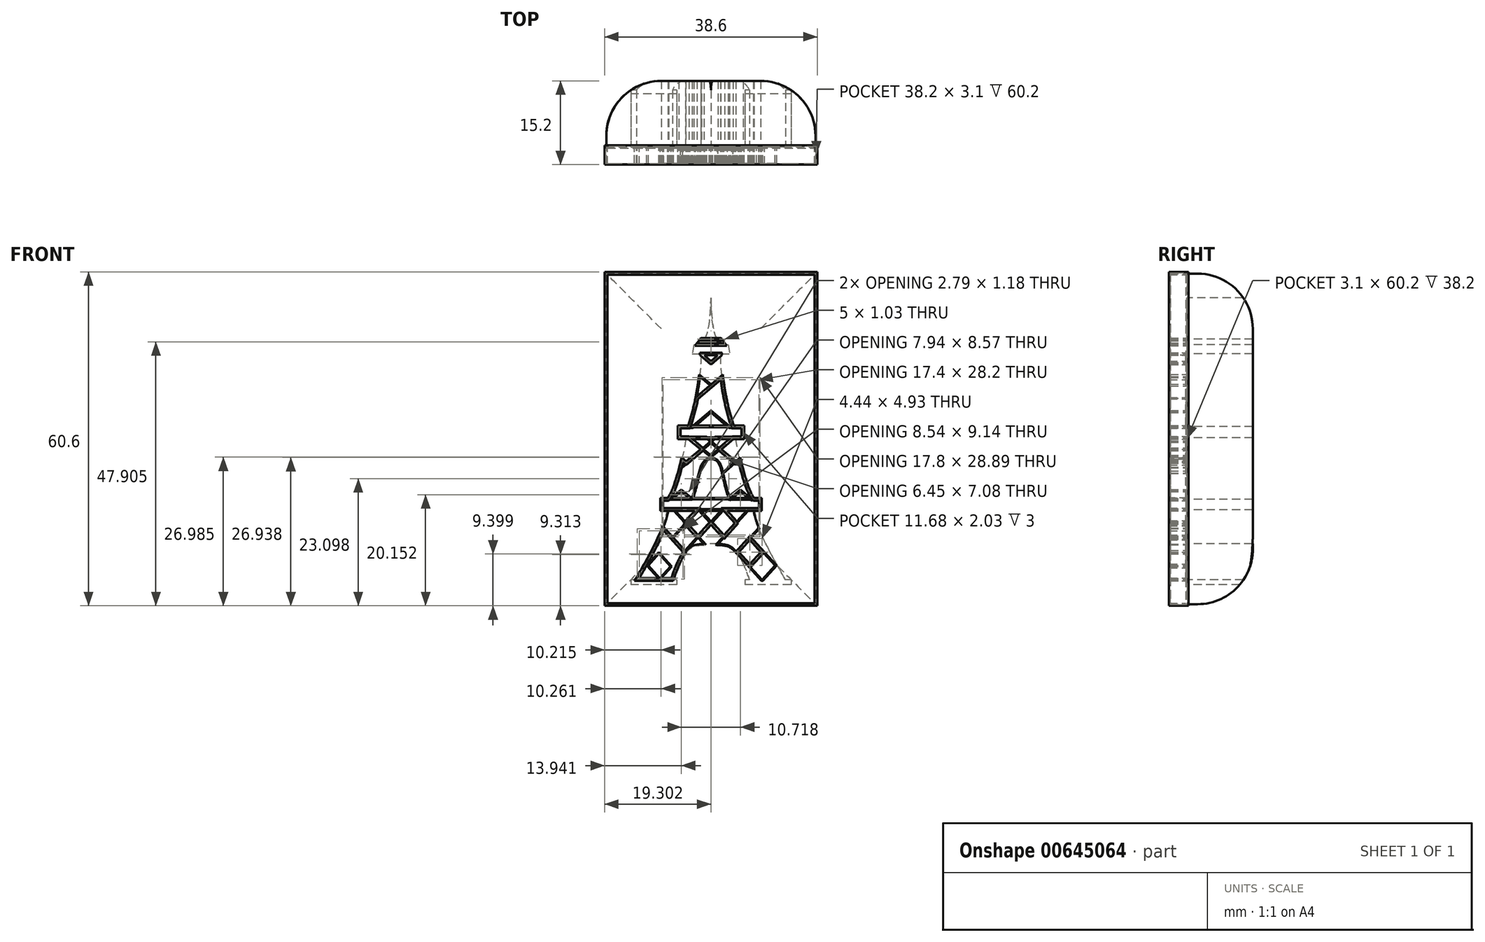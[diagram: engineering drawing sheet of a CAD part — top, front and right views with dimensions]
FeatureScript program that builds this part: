
annotation { "Feature Type Name" : "Feature", "Feature Type Description" : "" }
export const myFeature = defineFeature(function(context is Context, id is Id, definition is map)
    precondition{}
    {
        {
            var Q0;
            Q0=qCreatedBy(makeId("Front.planeOp"),FACE);
            var sketch = newSketch(context, id + "F0", { "sketchPlane" : qUnion([Q0])});
            skLineSegment(sketch, "E0.bottom", {"start": v(-9, 1.93) * mm, "end": v(9, 1.93) * mm});
            skLineSegment(sketch, "E0.top", {"start": v(-9, 0) * mm, "end": v(9, 0) * mm});
            skLineSegment(sketch, "E0.left", {"start": v(-9, 1.93) * mm, "end": v(-9, 0) * mm});
            skLineSegment(sketch, "E0.right", {"start": v(9, 1.93) * mm, "end": v(9, 0) * mm});
            skLineSegment(sketch, "E1.bottom", {"start": v(-5.84, 15.08) * mm, "end": v(5.84, 15.08) * mm});
            skLineSegment(sketch, "E1.top", {"start": v(-5.84, 13.05) * mm, "end": v(5.84, 13.05) * mm});
            skLineSegment(sketch, "E1.left", {"start": v(-5.84, 15.08) * mm, "end": v(-5.84, 13.05) * mm});
            skLineSegment(sketch, "E1.right", {"start": v(5.84, 15.08) * mm, "end": v(5.84, 13.05) * mm});
            skFitSpline(sketch, "E2", {"points": [v(-7.8, 1.93) * mm, v(-4.54, 13.05) * mm], "startDerivative": vector(4.67, 4.81) * mm, "endDerivative": vector(-0.3, 2.62) * mm});
            skFitSpline(sketch, "E3.MirrorCS", {"points": [v(7.8, 1.93) * mm, v(4.54, 13.05) * mm], "startDerivative": vector(-4.67, 4.81) * mm, "endDerivative": vector(0.3, 2.62) * mm});
            skFitSpline(sketch, "E4", {"points": [v(-3.5, 1.93) * mm, v(-1.06, 9.05) * mm, v(1.15, 9.05) * mm, v(3.51, 1.93) * mm], "startDerivative": vector(9.55, 27.67) * mm, "endDerivative": vector(10.37, -28.05) * mm});
            skPoint(sketch, "E5", {"position": v(0, 38.45) * mm});
            skPoint(sketch, "E6", {"position": v(0, -12.7) * mm});
            skLineSegment(sketch, "E7.bottom", {"start": v(-3.1, 29.96) * mm, "end": v(3.1, 29.96) * mm});
            skLineSegment(sketch, "E7.top", {"start": v(-3.4, 28.34) * mm, "end": v(3.4, 28.34) * mm});
            skLineSegment(sketch, "E8", {"start": v(-1.73, 30.99) * mm, "end": v(1.73, 30.99) * mm});
            skLineSegment(sketch, "E9", {"start": v(-2.5, 29.96) * mm, "end": v(2.5, 29.96) * mm});
            skLineSegment(sketch, "E10", {"start": v(-2.5, 29.96) * mm, "end": v(-1.73, 30.99) * mm});
            skLineSegment(sketch, "E11", {"start": v(1.73, 30.99) * mm, "end": v(2.5, 29.96) * mm});
            skFitSpline(sketch, "E12", {"points": [v(-1.28, 30.99) * mm, v(0, 38.45) * mm], "startDerivative": vector(2.63, 2) * mm, "endDerivative": vector(0.25, 11.2) * mm});
            skFitSpline(sketch, "E13.MirrorCS", {"points": [v(1.28, 30.99) * mm, v(0, 38.45) * mm], "startDerivative": vector(-2.63, 2) * mm, "endDerivative": vector(-0.25, 11.2) * mm});
            skLineSegment(sketch, "E14", {"start": v(-3.1, 29.96) * mm, "end": v(-3.4, 28.34) * mm});
            skLineSegment(sketch, "E15", {"start": v(3.1, 29.96) * mm, "end": v(3.4, 28.34) * mm});
            skFitSpline(sketch, "E16", {"points": [v(-4, 15.07) * mm, v(-1.8, 28.35) * mm], "startDerivative": vector(5.02, 14.78) * mm, "endDerivative": vector(-0.5, 7.77) * mm});
            skFitSpline(sketch, "E17.MirrorCS", {"points": [v(4, 15.07) * mm, v(1.8, 28.35) * mm], "startDerivative": vector(-5.02, 14.78) * mm, "endDerivative": vector(0.5, 7.77) * mm});
            skFitSpline(sketch, "E18", {"points": [v(-13.53, -12.7) * mm, v(-7.7, 0) * mm], "startDerivative": vector(10.31, 17.56) * mm, "endDerivative": vector(1.77, 9.43) * mm});
            skFitSpline(sketch, "E19", {"points": [v(-7, -12.7) * mm, v(-1.83, -6.23) * mm, v(1.83, -6.23) * mm, v(7, -12.7) * mm], "startDerivative": vector(16.22, 48.06) * mm, "endDerivative": vector(16.22, -48.06) * mm});
            skFitSpline(sketch, "E20.MirrorCS", {"points": [v(13.53, -12.7) * mm, v(7.7, 0) * mm], "startDerivative": vector(-10.31, 17.56) * mm, "endDerivative": vector(-1.77, 9.43) * mm});
            skLineSegment(sketch, "E21", {"start": v(-13.53, -12.7) * mm, "end": v(-7, -12.7) * mm});
            skLineSegment(sketch, "E22.bottom", {"start": v(-14.53, -12.7) * mm, "end": v(-6.2, -12.7) * mm});
            skLineSegment(sketch, "E22.top", {"start": v(-14.53, -13.6) * mm, "end": v(-6.2, -13.6) * mm});
            skLineSegment(sketch, "E22.left", {"start": v(-14.53, -12.7) * mm, "end": v(-14.53, -13.6) * mm});
            skLineSegment(sketch, "E22.right", {"start": v(-6.2, -12.7) * mm, "end": v(-6.2, -13.6) * mm});
            skLineSegment(sketch, "E23.MirrorCS", {"start": v(14.53, -12.7) * mm, "end": v(14.53, -13.6) * mm});
            skLineSegment(sketch, "E24.MirrorCS", {"start": v(14.53, -12.7) * mm, "end": v(6.2, -12.7) * mm});
            skLineSegment(sketch, "E25.MirrorCS", {"start": v(6.2, -12.7) * mm, "end": v(6.2, -13.6) * mm});
            skLineSegment(sketch, "E26.MirrorCS", {"start": v(14.53, -13.6) * mm, "end": v(6.2, -13.6) * mm});
            skLineSegment(sketch, "E27", {"start": v(-12.7, -11.28) * mm, "end": v(-2.52, 0) * mm});
            skLineSegment(sketch, "E28", {"start": v(-9.27, -12.7) * mm, "end": v(2.2, 0) * mm});
            skLineSegment(sketch, "E29", {"start": v(6.9, 0) * mm, "end": v(1.3, -6.2) * mm});
            skLineSegment(sketch, "E30", {"start": v(4.68, -7.7) * mm, "end": v(8.67, -3.27) * mm});
            skLineSegment(sketch, "E31", {"start": v(6.4, -11.02) * mm, "end": v(10.24, -6.76) * mm});
            skLineSegment(sketch, "E32.MirrorCS", {"start": v(12.7, -11.28) * mm, "end": v(2.52, 0) * mm});
            skLineSegment(sketch, "E33.MirrorCS", {"start": v(9.27, -12.7) * mm, "end": v(-2.2, 0) * mm});
            skLineSegment(sketch, "E34.MirrorCS", {"start": v(-6.9, 0) * mm, "end": v(-1.3, -6.2) * mm});
            skLineSegment(sketch, "E35.MirrorCS", {"start": v(-6.4, -11.02) * mm, "end": v(-10.24, -6.76) * mm});
            skLineSegment(sketch, "E36.MirrorCS", {"start": v(-4.68, -7.7) * mm, "end": v(-8.67, -3.27) * mm});
            skLineSegment(sketch, "E37", {"start": v(7, -12.7) * mm, "end": v(13.53, -12.7) * mm});
            skLineSegment(sketch, "E38", {"start": v(11.89, -9.85) * mm, "end": v(9.31, -12.7) * mm});
            skLineSegment(sketch, "E39.MirrorCS", {"start": v(-11.89, -9.85) * mm, "end": v(-9.31, -12.7) * mm});
            skLineSegment(sketch, "E40", {"start": v(-3.42, 1.93) * mm, "end": v(-6.5, 4.55) * mm});
            skLineSegment(sketch, "E41", {"start": v(-2.22, 6.61) * mm, "end": v(-5.22, 9.15) * mm});
            skLineSegment(sketch, "E42", {"start": v(0.27, 9.4) * mm, "end": v(-4.02, 13.05) * mm});
            skLineSegment(sketch, "E43", {"start": v(5.6, 7.62) * mm, "end": v(-0.8, 13.05) * mm});
            skLineSegment(sketch, "E44", {"start": v(2.33, 6.14) * mm, "end": v(7.3, 1.93) * mm});
            skLineSegment(sketch, "E45.MirrorCS", {"start": v(-2.33, 6.14) * mm, "end": v(-7.3, 1.93) * mm});
            skLineSegment(sketch, "E46.MirrorCS", {"start": v(-5.6, 7.62) * mm, "end": v(0.8, 13.05) * mm});
            skLineSegment(sketch, "E47.MirrorCS", {"start": v(-0.27, 9.4) * mm, "end": v(4.02, 13.05) * mm});
            skLineSegment(sketch, "E48.MirrorCS", {"start": v(2.22, 6.61) * mm, "end": v(5.22, 9.15) * mm});
            skLineSegment(sketch, "E49.MirrorCS", {"start": v(3.42, 1.93) * mm, "end": v(6.5, 4.55) * mm});
            skLineSegment(sketch, "E50", {"start": v(3.33, 15.08) * mm, "end": v(-2.64, 20.15) * mm});
            skLineSegment(sketch, "E51", {"start": v(2.62, 20.28) * mm, "end": v(-2, 24.2) * mm});
            skLineSegment(sketch, "E52", {"start": v(1.9, 25) * mm, "end": v(-1.8, 28.15) * mm});
            skLineSegment(sketch, "E53.MirrorCS", {"start": v(-1.9, 25) * mm, "end": v(1.8, 28.15) * mm});
            skLineSegment(sketch, "E54.MirrorCS", {"start": v(-3.33, 15.08) * mm, "end": v(2.64, 20.15) * mm});
            skLineSegment(sketch, "E55.MirrorCS", {"start": v(-2.62, 20.28) * mm, "end": v(2, 24.2) * mm});
            skLineSegment(sketch, "E56.bottom", {"start": v(-19, 42.87) * mm, "end": v(19, 42.87) * mm});
            skLineSegment(sketch, "E56.top", {"start": v(-19, -17.13) * mm, "end": v(19, -17.13) * mm});
            skLineSegment(sketch, "E56.left", {"start": v(-19, 42.87) * mm, "end": v(-19, -17.13) * mm});
            skLineSegment(sketch, "E56.right", {"start": v(19, 42.87) * mm, "end": v(19, -17.13) * mm});
            skSolve(sketch);
        }
        {
            var Q0;
            {var subQ0=sQuery(id+"F0.wireOp",EDGE,"E12");Q0=makeQuery(id+"F0.imprint","IMPRINT",FACE,{"disambiguationData":[TD([[makeQuery(id+"F0.imprint","IMPRINT",EDGE,{"derivedFrom":subQ0}),-1.0]])]});}
            var Q1;
            Q1=makeQuery(id+"F0.imprint","IMPRINT",FACE,{"disambiguationData":[TD([[makeQuery(id+"F0.imprint","IMPRINT",EDGE,{"derivedFrom":sQuery(id+"F0.wireOp",EDGE,"E7.bottom")}),-1.0]])]});
            var Q2;
            {var subQ5=sQuery(id+"F0.wireOp",EDGE,"E51");var subQ6=sQuery(id+"F0.wireOp",EDGE,"E16");var subQ7=makeQuery(id+"F0.imprint","INTERSECT",VERTEX,{"derivedFrom":[subQ6,subQ5]});Q2=makeQuery(id+"F0.imprint","IMPRINT",FACE,{"disambiguationData":[TD([[makeQuery(id+"F0.imprint","IMPRINT",EDGE,{"disambiguationData":[TD([[subQ7,-1.0]])],"derivedFrom":subQ6}),-1.0]])]});}
            var Q3;
            {var subQ5=sQuery(id+"F0.wireOp",EDGE,"E50");var subQ6=sQuery(id+"F0.wireOp",EDGE,"E16");var subQ7=makeQuery(id+"F0.imprint","INTERSECT",VERTEX,{"derivedFrom":[subQ6,subQ5]});Q3=makeQuery(id+"F0.imprint","IMPRINT",FACE,{"disambiguationData":[TD([[makeQuery(id+"F0.imprint","IMPRINT",EDGE,{"disambiguationData":[TD([[subQ7,-1.0]])],"derivedFrom":subQ6}),-1.0]])]});}
            var Q4;
            {var subQ0=sQuery(id+"F0.wireOp",EDGE,"E50");var subQ1=sQuery(id+"F0.wireOp",EDGE,"E1.bottom");var subQ2=makeQuery(id+"F0.imprint","INTERSECT",VERTEX,{"derivedFrom":[subQ1,subQ0]});Q4=makeQuery(id+"F0.imprint","IMPRINT",FACE,{"disambiguationData":[TD([[makeQuery(id+"F0.imprint","IMPRINT",EDGE,{"disambiguationData":[TD([[subQ2,1.0]])],"derivedFrom":subQ1}),1.0]])]});}
            var Q5;
            {var subQ0=sQuery(id+"F0.wireOp",EDGE,"E43");var subQ1=sQuery(id+"F0.wireOp",EDGE,"E1.top");var subQ2=makeQuery(id+"F0.imprint","INTERSECT",VERTEX,{"derivedFrom":[subQ1,subQ0]});Q5=makeQuery(id+"F0.imprint","IMPRINT",FACE,{"disambiguationData":[TD([[makeQuery(id+"F0.imprint","IMPRINT",EDGE,{"disambiguationData":[TD([[subQ2,-1.0]])],"derivedFrom":subQ1}),-1.0]])]});}
            var Q6;
            {var subQ1=sQuery(id+"F0.wireOp",EDGE,"E2");var subQ6=sQuery(id+"F0.wireOp",EDGE,"E1.top");var subQ9=makeQuery(id+"F0.imprint","INTERSECT",VERTEX,{"derivedFrom":[subQ6,subQ1]});Q6=makeQuery(id+"F0.imprint","IMPRINT",FACE,{"disambiguationData":[TD([[makeQuery(id+"F0.imprint","IMPRINT",EDGE,{"disambiguationData":[TD([[subQ9,-1.0]])],"derivedFrom":subQ6}),-1.0]])]});}
            var Q7;
            {var subQ0=sQuery(id+"F0.wireOp",EDGE,"E47.MirrorCS");var subQ1=sQuery(id+"F0.wireOp",EDGE,"E42");var subQ2=makeQuery(id+"F0.imprint","INTERSECT",VERTEX,{"derivedFrom":[subQ1,subQ0]});Q7=makeQuery(id+"F0.imprint","IMPRINT",FACE,{"disambiguationData":[TD([[makeQuery(id+"F0.imprint","IMPRINT",EDGE,{"disambiguationData":[TD([[subQ2,-1.0]])],"derivedFrom":subQ1}),-1.0]])]});}
            var Q8;
            {var subQ5=sQuery(id+"F0.wireOp",EDGE,"E1.top");var subQ7=sQuery(id+"F0.wireOp",EDGE,"E3.MirrorCS");var subQ8=makeQuery(id+"F0.imprint","INTERSECT",VERTEX,{"derivedFrom":[subQ5,subQ7]});Q8=makeQuery(id+"F0.imprint","IMPRINT",FACE,{"disambiguationData":[TD([[makeQuery(id+"F0.imprint","IMPRINT",EDGE,{"disambiguationData":[TD([[subQ8,1.0]])],"derivedFrom":subQ5}),-1.0]])]});}
            var Q9;
            {var subQ0=sQuery(id+"F0.wireOp",EDGE,"E4");var subQ1=sQuery(id+"F0.wireOp",EDGE,"E0.bottom");var subQ2=makeQuery(id+"F0.imprint","INTERSECT",VERTEX,{"disambiguationData":[OD(1.0)],"derivedFrom":[subQ1,subQ0]});Q9=makeQuery(id+"F0.imprint","IMPRINT",FACE,{"disambiguationData":[TD([[makeQuery(id+"F0.imprint","IMPRINT",EDGE,{"disambiguationData":[TD([[subQ2,-1.0]])],"derivedFrom":subQ1}),1.0]])]});}
            var Q10;
            {var subQ0=sQuery(id+"F0.wireOp",EDGE,"E4");var subQ1=sQuery(id+"F0.wireOp",EDGE,"E0.bottom");var subQ2=makeQuery(id+"F0.imprint","INTERSECT",VERTEX,{"disambiguationData":[OD(0.0)],"derivedFrom":[subQ1,subQ0]});Q10=makeQuery(id+"F0.imprint","IMPRINT",FACE,{"disambiguationData":[TD([[makeQuery(id+"F0.imprint","IMPRINT",EDGE,{"disambiguationData":[TD([[subQ2,1.0]])],"derivedFrom":subQ1}),1.0]])]});}
            var Q11;
            {var subQ0=sQuery(id+"F0.wireOp",EDGE,"E27");var subQ1=sQuery(id+"F0.wireOp",EDGE,"E0.top");var subQ2=makeQuery(id+"F0.imprint","INTERSECT",VERTEX,{"derivedFrom":[subQ1,subQ0]});Q11=makeQuery(id+"F0.imprint","IMPRINT",FACE,{"disambiguationData":[TD([[makeQuery(id+"F0.imprint","IMPRINT",EDGE,{"disambiguationData":[TD([[subQ2,1.0]])],"derivedFrom":subQ1}),-1.0]])]});}
            var Q12;
            {var subQ0=sQuery(id+"F0.wireOp",EDGE,"E29");var subQ1=sQuery(id+"F0.wireOp",EDGE,"E0.top");var subQ2=makeQuery(id+"F0.imprint","INTERSECT",VERTEX,{"derivedFrom":[subQ1,subQ0]});Q12=makeQuery(id+"F0.imprint","IMPRINT",FACE,{"disambiguationData":[TD([[makeQuery(id+"F0.imprint","IMPRINT",EDGE,{"disambiguationData":[TD([[subQ2,1.0]])],"derivedFrom":subQ1}),-1.0]])]});}
            var Q13;
            {var subQ0=sQuery(id+"F0.wireOp",EDGE,"E32.MirrorCS");var subQ1=sQuery(id+"F0.wireOp",EDGE,"E29");var subQ2=makeQuery(id+"F0.imprint","INTERSECT",VERTEX,{"derivedFrom":[subQ1,subQ0]});Q13=makeQuery(id+"F0.imprint","IMPRINT",FACE,{"disambiguationData":[TD([[makeQuery(id+"F0.imprint","IMPRINT",EDGE,{"disambiguationData":[TD([[subQ2,-1.0]])],"derivedFrom":subQ1}),1.0]])]});}
            var Q14;
            {var subQ0=sQuery(id+"F0.wireOp",EDGE,"E28");var subQ1=sQuery(id+"F0.wireOp",EDGE,"E0.top");var subQ2=makeQuery(id+"F0.imprint","INTERSECT",VERTEX,{"derivedFrom":[subQ1,subQ0]});Q14=makeQuery(id+"F0.imprint","IMPRINT",FACE,{"disambiguationData":[TD([[makeQuery(id+"F0.imprint","IMPRINT",EDGE,{"disambiguationData":[TD([[subQ2,1.0]])],"derivedFrom":subQ1}),-1.0]])]});}
            var Q15;
            {var subQ0=sQuery(id+"F0.wireOp",EDGE,"E35.MirrorCS");var subQ1=sQuery(id+"F0.wireOp",EDGE,"E18");var subQ2=makeQuery(id+"F0.imprint","INTERSECT",VERTEX,{"derivedFrom":[subQ1,subQ0]});Q15=makeQuery(id+"F0.imprint","IMPRINT",FACE,{"disambiguationData":[TD([[makeQuery(id+"F0.imprint","IMPRINT",EDGE,{"disambiguationData":[TD([[subQ2,-1.0]])],"derivedFrom":subQ1}),-1.0]])]});}
            var Q16;
            {var subQ0=sQuery(id+"F0.wireOp",EDGE,"E36.MirrorCS");var subQ1=sQuery(id+"F0.wireOp",EDGE,"E27");var subQ2=makeQuery(id+"F0.imprint","INTERSECT",VERTEX,{"derivedFrom":[subQ1,subQ0]});Q16=makeQuery(id+"F0.imprint","IMPRINT",FACE,{"disambiguationData":[TD([[makeQuery(id+"F0.imprint","IMPRINT",EDGE,{"disambiguationData":[TD([[subQ2,-1.0]])],"derivedFrom":subQ1}),-1.0]])]});}
            var Q17;
            {var subQ3=sQuery(id+"F0.wireOp",EDGE,"E29");var subQ5=sQuery(id+"F0.wireOp",EDGE,"E19");var subQ6=makeQuery(id+"F0.imprint","INTERSECT",VERTEX,{"derivedFrom":[subQ5,subQ3]});Q17=makeQuery(id+"F0.imprint","IMPRINT",FACE,{"disambiguationData":[TD([[makeQuery(id+"F0.imprint","IMPRINT",EDGE,{"disambiguationData":[TD([[subQ6,1.0]])],"derivedFrom":subQ5}),1.0]])]});}
            var Q18;
            {var subQ0=sQuery(id+"F0.wireOp",EDGE,"E30");var subQ1=sQuery(id+"F0.wireOp",EDGE,"E20.MirrorCS");var subQ2=makeQuery(id+"F0.imprint","INTERSECT",VERTEX,{"derivedFrom":[subQ1,subQ0]});Q18=makeQuery(id+"F0.imprint","IMPRINT",FACE,{"disambiguationData":[TD([[makeQuery(id+"F0.imprint","IMPRINT",EDGE,{"disambiguationData":[TD([[subQ2,1.0]])],"derivedFrom":subQ1}),1.0]])]});}
            var Q19;
            {var subQ3=sQuery(id+"F0.wireOp",EDGE,"E28");var subQ5=sQuery(id+"F0.wireOp",EDGE,"E22.bottom");var subQ6=makeQuery(id+"F0.imprint","INTERSECT",VERTEX,{"derivedFrom":[subQ5,subQ3]});Q19=makeQuery(id+"F0.imprint","IMPRINT",FACE,{"disambiguationData":[TD([[makeQuery(id+"F0.imprint","IMPRINT",EDGE,{"disambiguationData":[TD([[subQ6,1.0]])],"derivedFrom":subQ5}),1.0]])]});}
            var Q20;
            {var subQ0=sQuery(id+"F0.wireOp",EDGE,"E35.MirrorCS");var subQ1=sQuery(id+"F0.wireOp",EDGE,"E19");var subQ2=makeQuery(id+"F0.imprint","INTERSECT",VERTEX,{"derivedFrom":[subQ1,subQ0]});Q20=makeQuery(id+"F0.imprint","IMPRINT",FACE,{"disambiguationData":[TD([[makeQuery(id+"F0.imprint","IMPRINT",EDGE,{"disambiguationData":[TD([[subQ2,-1.0]])],"derivedFrom":subQ1}),1.0]])]});}
            var Q21;
            {var subQ0=sQuery(id+"F0.wireOp",EDGE,"E30");var subQ1=sQuery(id+"F0.wireOp",EDGE,"E19");var subQ2=makeQuery(id+"F0.imprint","INTERSECT",VERTEX,{"derivedFrom":[subQ1,subQ0]});Q21=makeQuery(id+"F0.imprint","IMPRINT",FACE,{"disambiguationData":[TD([[makeQuery(id+"F0.imprint","IMPRINT",EDGE,{"disambiguationData":[TD([[subQ2,-1.0]])],"derivedFrom":subQ1}),1.0]])]});}
            var Q22;
            {var subQ1=sQuery(id+"F0.wireOp",EDGE,"E33.MirrorCS");var subQ5=sQuery(id+"F0.wireOp",EDGE,"E31");var subQ6=makeQuery(id+"F0.imprint","INTERSECT",VERTEX,{"derivedFrom":[subQ5,subQ1]});Q22=makeQuery(id+"F0.imprint","IMPRINT",FACE,{"disambiguationData":[TD([[makeQuery(id+"F0.imprint","IMPRINT",EDGE,{"disambiguationData":[TD([[subQ6,-1.0]])],"derivedFrom":subQ5}),-1.0]])]});}
            var Q23;
            {var subQ0=sQuery(id+"F0.wireOp",EDGE,"E32.MirrorCS");var subQ1=sQuery(id+"F0.wireOp",EDGE,"E20.MirrorCS");var subQ2=makeQuery(id+"F0.imprint","INTERSECT",VERTEX,{"derivedFrom":[subQ1,subQ0]});Q23=makeQuery(id+"F0.imprint","IMPRINT",FACE,{"disambiguationData":[TD([[makeQuery(id+"F0.imprint","IMPRINT",EDGE,{"disambiguationData":[TD([[subQ2,-1.0]])],"derivedFrom":subQ1}),1.0]])]});}
            var Q24;
            {var subQ0=sQuery(id+"F0.wireOp",EDGE,"E27");var subQ1=sQuery(id+"F0.wireOp",EDGE,"E18");var subQ2=makeQuery(id+"F0.imprint","INTERSECT",VERTEX,{"derivedFrom":[subQ1,subQ0]});Q24=makeQuery(id+"F0.imprint","IMPRINT",FACE,{"disambiguationData":[TD([[makeQuery(id+"F0.imprint","IMPRINT",EDGE,{"disambiguationData":[TD([[subQ2,-1.0]])],"derivedFrom":subQ1}),-1.0]])]});}
            var Q25;
            Q25=makeQuery(id+"F0.imprint","IMPRINT",FACE,{"disambiguationData":[TD([[makeQuery(id+"F0.imprint","IMPRINT",EDGE,{"derivedFrom":sQuery(id+"F0.wireOp",EDGE,"E22.top")}),1.0]])]});
            var Q26;
            {var subQ5=sQuery(id+"F0.wireOp",EDGE,"E23.MirrorCS");Q26=makeQuery(id+"F0.imprint","IMPRINT",FACE,{"disambiguationData":[TD([[makeQuery(id+"F0.imprint","IMPRINT",EDGE,{"derivedFrom":subQ5}),-1.0]])]});}
            extrude(context, id + "F1", {"entities" : qUnion([Q0, Q1, Q2, Q3, Q4, Q5, Q6, Q7, Q8, Q9, Q10, Q11, Q12, Q13, Q14, Q15, Q16, Q17, Q18, Q19, Q20, Q21, Q22, Q23, Q24, Q25, Q26]), "depth" : 3 * mm, "offsetDistance" : 25 * mm});
        }
        {
            var Q0;
            Q0=makeQuery(id+"F1.opExtrude","CAP_FACE",FACE,{"disambiguationData":[OSD([sQuery(id+"F0.wireOp",EDGE,"E27"),sQuery(id+"F0.wireOp",EDGE,"E28"),sQuery(id+"F0.wireOp",EDGE,"E34.MirrorCS"),sQuery(id+"F0.wireOp",EDGE,"E36.MirrorCS")])],"isStart":false});
            var Q1;
            Q1=makeQuery(id+"F1.opExtrude","CAP_FACE",FACE,{"disambiguationData":[OSD([sQuery(id+"F0.wireOp",EDGE,"E0.top"),sQuery(id+"F0.wireOp",EDGE,"E27"),sQuery(id+"F0.wireOp",EDGE,"E34.MirrorCS")])],"isStart":false});
            var Q2;
            Q2=makeQuery(id+"F1.opExtrude","CAP_FACE",FACE,{"disambiguationData":[OSD([sQuery(id+"F0.wireOp",EDGE,"E0.top"),sQuery(id+"F0.wireOp",EDGE,"E28"),sQuery(id+"F0.wireOp",EDGE,"E33.MirrorCS")])],"isStart":false});
            var Q3;
            Q3=makeQuery(id+"F1.opExtrude","CAP_FACE",FACE,{"disambiguationData":[OSD([sQuery(id+"F0.wireOp",EDGE,"E0.bottom"),sQuery(id+"F0.wireOp",EDGE,"E4"),sQuery(id+"F0.wireOp",EDGE,"E40"),sQuery(id+"F0.wireOp",EDGE,"E45.MirrorCS")])],"isStart":false});
            var Q4;
            Q4=makeQuery(id+"F1.opExtrude","CAP_FACE",FACE,{"disambiguationData":[OSD([sQuery(id+"F0.wireOp",EDGE,"E0.bottom"),sQuery(id+"F0.wireOp",EDGE,"E4"),sQuery(id+"F0.wireOp",EDGE,"E44"),sQuery(id+"F0.wireOp",EDGE,"E49.MirrorCS")])],"isStart":false});
            var Q5;
            Q5=makeQuery(id+"F1.opExtrude","CAP_FACE",FACE,{"disambiguationData":[OSD([sQuery(id+"F0.wireOp",EDGE,"E42"),sQuery(id+"F0.wireOp",EDGE,"E43"),sQuery(id+"F0.wireOp",EDGE,"E46.MirrorCS"),sQuery(id+"F0.wireOp",EDGE,"E47.MirrorCS")])],"isStart":false});
            var Q6;
            Q6=makeQuery(id+"F1.opExtrude","CAP_FACE",FACE,{"disambiguationData":[OSD([sQuery(id+"F0.wireOp",EDGE,"E1.top"),sQuery(id+"F0.wireOp",EDGE,"E43"),sQuery(id+"F0.wireOp",EDGE,"E46.MirrorCS")])],"isStart":false});
            var Q7;
            Q7=makeQuery(id+"F1.opExtrude","CAP_FACE",FACE,{"disambiguationData":[OSD([sQuery(id+"F0.wireOp",EDGE,"E19"),sQuery(id+"F0.wireOp",EDGE,"E28"),sQuery(id+"F0.wireOp",EDGE,"E29"),sQuery(id+"F0.wireOp",EDGE,"E33.MirrorCS"),sQuery(id+"F0.wireOp",EDGE,"E34.MirrorCS")])],"isStart":false});
            var Q8;
            Q8=makeQuery(id+"F1.opExtrude","CAP_FACE",FACE,{"disambiguationData":[OSD([sQuery(id+"F0.wireOp",EDGE,"E29"),sQuery(id+"F0.wireOp",EDGE,"E30"),sQuery(id+"F0.wireOp",EDGE,"E32.MirrorCS"),sQuery(id+"F0.wireOp",EDGE,"E33.MirrorCS")])],"isStart":false});
            var Q9;
            Q9=makeQuery(id+"F1.opExtrude","CAP_FACE",FACE,{"disambiguationData":[OSD([sQuery(id+"F0.wireOp",EDGE,"E18"),sQuery(id+"F0.wireOp",EDGE,"E27"),sQuery(id+"F0.wireOp",EDGE,"E35.MirrorCS"),sQuery(id+"F0.wireOp",EDGE,"E36.MirrorCS")])],"isStart":false});
            var Q10;
            Q10=makeQuery(id+"F1.opExtrude","CAP_FACE",FACE,{"disambiguationData":[OSD([sQuery(id+"F0.wireOp",EDGE,"E20.MirrorCS"),sQuery(id+"F0.wireOp",EDGE,"E30"),sQuery(id+"F0.wireOp",EDGE,"E31"),sQuery(id+"F0.wireOp",EDGE,"E32.MirrorCS")])],"isStart":false});
            var Q11;
            Q11=makeQuery(id+"F1.opExtrude","CAP_FACE",FACE,{"disambiguationData":[OSD([sQuery(id+"F0.wireOp",EDGE,"E19"),sQuery(id+"F0.wireOp",EDGE,"E30"),sQuery(id+"F0.wireOp",EDGE,"E31"),sQuery(id+"F0.wireOp",EDGE,"E33.MirrorCS")])],"isStart":false});
            var Q12;
            Q12=makeQuery(id+"F1.opExtrude","CAP_FACE",FACE,{"disambiguationData":[OSD([sQuery(id+"F0.wireOp",EDGE,"E23.MirrorCS"),sQuery(id+"F0.wireOp",EDGE,"E24.MirrorCS"),sQuery(id+"F0.wireOp",EDGE,"E25.MirrorCS"),sQuery(id+"F0.wireOp",EDGE,"E26.MirrorCS"),sQuery(id+"F0.wireOp",EDGE,"E31"),sQuery(id+"F0.wireOp",EDGE,"E32.MirrorCS"),sQuery(id+"F0.wireOp",EDGE,"E33.MirrorCS"),sQuery(id+"F0.wireOp",EDGE,"E37"),sQuery(id+"F0.wireOp",EDGE,"E38")])],"isStart":false});
            var Q13;
            Q13=makeQuery(id+"F1.opExtrude","CAP_FACE",FACE,{"disambiguationData":[OSD([sQuery(id+"F0.wireOp",EDGE,"E20.MirrorCS"),sQuery(id+"F0.wireOp",EDGE,"E32.MirrorCS"),sQuery(id+"F0.wireOp",EDGE,"E38")])],"isStart":false});
            var Q14;
            Q14=makeQuery(id+"F1.opExtrude","CAP_FACE",FACE,{"disambiguationData":[OSD([sQuery(id+"F0.wireOp",EDGE,"E22.bottom"),sQuery(id+"F0.wireOp",EDGE,"E22.top"),sQuery(id+"F0.wireOp",EDGE,"E22.left"),sQuery(id+"F0.wireOp",EDGE,"E22.right"),sQuery(id+"F0.wireOp",EDGE,"E27"),sQuery(id+"F0.wireOp",EDGE,"E28"),sQuery(id+"F0.wireOp",EDGE,"E35.MirrorCS"),sQuery(id+"F0.wireOp",EDGE,"E39.MirrorCS")])],"isStart":false});
            var Q15;
            Q15=makeQuery(id+"F1.opExtrude","CAP_FACE",FACE,{"disambiguationData":[OSD([sQuery(id+"F0.wireOp",EDGE,"E18"),sQuery(id+"F0.wireOp",EDGE,"E27"),sQuery(id+"F0.wireOp",EDGE,"E39.MirrorCS")])],"isStart":false});
            var Q16;
            Q16=makeQuery(id+"F1.opExtrude","CAP_FACE",FACE,{"disambiguationData":[OSD([sQuery(id+"F0.wireOp",EDGE,"E19"),sQuery(id+"F0.wireOp",EDGE,"E28"),sQuery(id+"F0.wireOp",EDGE,"E35.MirrorCS"),sQuery(id+"F0.wireOp",EDGE,"E36.MirrorCS")])],"isStart":false});
            var Q17;
            Q17=makeQuery(id+"F1.opExtrude","CAP_FACE",FACE,{"disambiguationData":[OSD([sQuery(id+"F0.wireOp",EDGE,"E1.bottom"),sQuery(id+"F0.wireOp",EDGE,"E50"),sQuery(id+"F0.wireOp",EDGE,"E54.MirrorCS")])],"isStart":false});
            var Q18;
            Q18=makeQuery(id+"F1.opExtrude","CAP_FACE",FACE,{"disambiguationData":[OSD([sQuery(id+"F0.wireOp",EDGE,"E16"),sQuery(id+"F0.wireOp",EDGE,"E17.MirrorCS"),sQuery(id+"F0.wireOp",EDGE,"E50"),sQuery(id+"F0.wireOp",EDGE,"E51"),sQuery(id+"F0.wireOp",EDGE,"E54.MirrorCS"),sQuery(id+"F0.wireOp",EDGE,"E55.MirrorCS")])],"isStart":false});
            var Q19;
            Q19=makeQuery(id+"F1.opExtrude","CAP_FACE",FACE,{"disambiguationData":[OSD([sQuery(id+"F0.wireOp",EDGE,"E16"),sQuery(id+"F0.wireOp",EDGE,"E17.MirrorCS"),sQuery(id+"F0.wireOp",EDGE,"E51"),sQuery(id+"F0.wireOp",EDGE,"E52"),sQuery(id+"F0.wireOp",EDGE,"E53.MirrorCS"),sQuery(id+"F0.wireOp",EDGE,"E55.MirrorCS")])],"isStart":false});
            var Q20;
            Q20=makeQuery(id+"F1.opExtrude","CAP_FACE",FACE,{"disambiguationData":[OSD([sQuery(id+"F0.wireOp",EDGE,"E7.bottom"),sQuery(id+"F0.wireOp",EDGE,"E7.top"),sQuery(id+"F0.wireOp",EDGE,"E14"),sQuery(id+"F0.wireOp",EDGE,"E15")])],"isStart":false});
            var Q21;
            Q21=makeQuery(id+"F1.opExtrude","CAP_FACE",FACE,{"disambiguationData":[OSD([sQuery(id+"F0.wireOp",EDGE,"E8"),sQuery(id+"F0.wireOp",EDGE,"E12"),sQuery(id+"F0.wireOp",EDGE,"E13.MirrorCS")])],"isStart":false});
            shell(context, id + "F2", {"entities" : qUnion([Q0, Q1, Q2, Q3, Q4, Q5, Q6, Q7, Q8, Q9, Q10, Q11, Q12, Q13, Q14, Q15, Q16, Q17, Q18, Q19, Q20, Q21]), "thickness" : 0.1 * mm, "oppositeDirection" : true});
        }
        {
            var Q0;
            Q0=makeQuery(id+"F1.opExtrude","CAP_FACE",FACE,{"disambiguationData":[OSD([sQuery(id+"F0.wireOp",EDGE,"E1.top"),sQuery(id+"F0.wireOp",EDGE,"E2"),sQuery(id+"F0.wireOp",EDGE,"E41"),sQuery(id+"F0.wireOp",EDGE,"E42"),sQuery(id+"F0.wireOp",EDGE,"E46.MirrorCS")])],"isStart":false});
            var Q1;
            Q1=makeQuery(id+"F1.opExtrude","CAP_FACE",FACE,{"disambiguationData":[OSD([sQuery(id+"F0.wireOp",EDGE,"E1.top"),sQuery(id+"F0.wireOp",EDGE,"E3.MirrorCS"),sQuery(id+"F0.wireOp",EDGE,"E43"),sQuery(id+"F0.wireOp",EDGE,"E47.MirrorCS"),sQuery(id+"F0.wireOp",EDGE,"E48.MirrorCS")])],"isStart":false});
            shell(context, id + "F3", {"entities" : qUnion([Q0, Q1]), "thickness" : 0.2 * mm, "oppositeDirection" : true});
        }
        {
            var Q0;
            {var subQ0=sQuery(id+"F0.wireOp",EDGE,"E33.MirrorCS");var subQ1=sQuery(id+"F0.wireOp",EDGE,"E30");var subQ2=makeQuery(id+"F0.imprint","INTERSECT",VERTEX,{"derivedFrom":[subQ1,subQ0]});Q0=makeQuery(id+"F0.imprint","IMPRINT",FACE,{"disambiguationData":[TD([[makeQuery(id+"F0.imprint","IMPRINT",EDGE,{"disambiguationData":[TD([[subQ2,-1.0]])],"derivedFrom":subQ1}),-1.0]])]});}
            var Q1;
            {var subQ1=sQuery(id+"F0.wireOp",EDGE,"E19");var subQ3=sQuery(id+"F0.wireOp",EDGE,"E31");var subQ4=makeQuery(id+"F0.imprint","INTERSECT",VERTEX,{"derivedFrom":[subQ1,subQ3]});Q1=makeQuery(id+"F0.imprint","IMPRINT",FACE,{"disambiguationData":[TD([[makeQuery(id+"F0.imprint","IMPRINT",EDGE,{"disambiguationData":[TD([[subQ4,-1.0]])],"derivedFrom":subQ3}),-1.0]])]});}
            var Q2;
            {var subQ1=sQuery(id+"F0.wireOp",EDGE,"E20.MirrorCS");var subQ3=sQuery(id+"F0.wireOp",EDGE,"E32.MirrorCS");var subQ4=makeQuery(id+"F0.imprint","INTERSECT",VERTEX,{"derivedFrom":[subQ1,subQ3]});Q2=makeQuery(id+"F0.imprint","IMPRINT",FACE,{"disambiguationData":[TD([[makeQuery(id+"F0.imprint","IMPRINT",EDGE,{"disambiguationData":[TD([[subQ4,-1.0]])],"derivedFrom":subQ3}),1.0]])]});}
            var Q3;
            {var subQ0=sQuery(id+"F0.wireOp",EDGE,"E31");var subQ1=sQuery(id+"F0.wireOp",EDGE,"E20.MirrorCS");var subQ2=makeQuery(id+"F0.imprint","INTERSECT",VERTEX,{"derivedFrom":[subQ1,subQ0]});Q3=makeQuery(id+"F0.imprint","IMPRINT",FACE,{"disambiguationData":[TD([[makeQuery(id+"F0.imprint","IMPRINT",EDGE,{"disambiguationData":[TD([[subQ2,1.0]])],"derivedFrom":subQ1}),1.0]])]});}
            var Q4;
            {var subQ0=sQuery(id+"F0.wireOp",EDGE,"E20.MirrorCS");var subQ1=sQuery(id+"F0.wireOp",EDGE,"E0.top");var subQ2=makeQuery(id+"F0.imprint","INTERSECT",VERTEX,{"derivedFrom":[subQ1,subQ0]});Q4=makeQuery(id+"F0.imprint","IMPRINT",FACE,{"disambiguationData":[TD([[makeQuery(id+"F0.imprint","IMPRINT",EDGE,{"disambiguationData":[TD([[subQ2,1.0]])],"derivedFrom":subQ1}),-1.0]])]});}
            var Q5;
            {var subQ5=sQuery(id+"F0.wireOp",EDGE,"E28");var subQ6=sQuery(id+"F0.wireOp",EDGE,"E0.top");var subQ7=makeQuery(id+"F0.imprint","INTERSECT",VERTEX,{"derivedFrom":[subQ6,subQ5]});Q5=makeQuery(id+"F0.imprint","IMPRINT",FACE,{"disambiguationData":[TD([[makeQuery(id+"F0.imprint","IMPRINT",EDGE,{"disambiguationData":[TD([[subQ7,-1.0]])],"derivedFrom":subQ6}),-1.0]])]});}
            var Q6;
            {var subQ0=sQuery(id+"F0.wireOp",EDGE,"E29");var subQ1=sQuery(id+"F0.wireOp",EDGE,"E19");var subQ2=makeQuery(id+"F0.imprint","INTERSECT",VERTEX,{"derivedFrom":[subQ1,subQ0]});Q6=makeQuery(id+"F0.imprint","IMPRINT",FACE,{"disambiguationData":[TD([[makeQuery(id+"F0.imprint","IMPRINT",EDGE,{"disambiguationData":[TD([[subQ2,-1.0]])],"derivedFrom":subQ1}),1.0]])]});}
            var Q7;
            {var subQ0=sQuery(id+"F0.wireOp",EDGE,"E34.MirrorCS");var subQ1=sQuery(id+"F0.wireOp",EDGE,"E19");var subQ2=makeQuery(id+"F0.imprint","INTERSECT",VERTEX,{"derivedFrom":[subQ1,subQ0]});Q7=makeQuery(id+"F0.imprint","IMPRINT",FACE,{"disambiguationData":[TD([[makeQuery(id+"F0.imprint","IMPRINT",EDGE,{"disambiguationData":[TD([[subQ2,1.0]])],"derivedFrom":subQ1}),1.0]])]});}
            var Q8;
            {var subQ1=sQuery(id+"F0.wireOp",EDGE,"E0.top");var subQ7=sQuery(id+"F0.wireOp",EDGE,"E27");var subQ9=makeQuery(id+"F0.imprint","INTERSECT",VERTEX,{"derivedFrom":[subQ1,subQ7]});Q8=makeQuery(id+"F0.imprint","IMPRINT",FACE,{"disambiguationData":[TD([[makeQuery(id+"F0.imprint","IMPRINT",EDGE,{"disambiguationData":[TD([[subQ9,-1.0]])],"derivedFrom":subQ1}),-1.0]])]});}
            var Q9;
            {var subQ5=sQuery(id+"F0.wireOp",EDGE,"E18");var subQ6=sQuery(id+"F0.wireOp",EDGE,"E0.top");var subQ7=makeQuery(id+"F0.imprint","INTERSECT",VERTEX,{"derivedFrom":[subQ6,subQ5]});Q9=makeQuery(id+"F0.imprint","IMPRINT",FACE,{"disambiguationData":[TD([[makeQuery(id+"F0.imprint","IMPRINT",EDGE,{"disambiguationData":[TD([[subQ7,-1.0]])],"derivedFrom":subQ6}),-1.0]])]});}
            var Q10;
            {var subQ0=sQuery(id+"F0.wireOp",EDGE,"E35.MirrorCS");var subQ1=sQuery(id+"F0.wireOp",EDGE,"E18");var subQ2=makeQuery(id+"F0.imprint","INTERSECT",VERTEX,{"derivedFrom":[subQ1,subQ0]});Q10=makeQuery(id+"F0.imprint","IMPRINT",FACE,{"disambiguationData":[TD([[makeQuery(id+"F0.imprint","IMPRINT",EDGE,{"disambiguationData":[TD([[subQ2,1.0]])],"derivedFrom":subQ1}),-1.0]])]});}
            var Q11;
            {var subQ0=sQuery(id+"F0.wireOp",EDGE,"E35.MirrorCS");var subQ1=sQuery(id+"F0.wireOp",EDGE,"E27");var subQ2=makeQuery(id+"F0.imprint","INTERSECT",VERTEX,{"derivedFrom":[subQ1,subQ0]});Q11=makeQuery(id+"F0.imprint","IMPRINT",FACE,{"disambiguationData":[TD([[makeQuery(id+"F0.imprint","IMPRINT",EDGE,{"disambiguationData":[TD([[subQ2,-1.0]])],"derivedFrom":subQ1}),-1.0]])]});}
            var Q12;
            {var subQ0=sQuery(id+"F0.wireOp",EDGE,"E22.bottom");var subQ1=sQuery(id+"F0.wireOp",EDGE,"E19");var subQ2=makeQuery(id+"F0.imprint","INTERSECT",VERTEX,{"derivedFrom":[subQ1,subQ0]});Q12=makeQuery(id+"F0.imprint","IMPRINT",FACE,{"disambiguationData":[TD([[makeQuery(id+"F0.imprint","IMPRINT",EDGE,{"disambiguationData":[TD([[subQ2,-1.0]])],"derivedFrom":subQ1}),1.0]])]});}
            var Q13;
            {var subQ0=sQuery(id+"F0.wireOp",EDGE,"E22.bottom");var subQ1=sQuery(id+"F0.wireOp",EDGE,"E18");var subQ2=makeQuery(id+"F0.imprint","INTERSECT",VERTEX,{"derivedFrom":[subQ1,subQ0]});Q13=makeQuery(id+"F0.imprint","IMPRINT",FACE,{"disambiguationData":[TD([[makeQuery(id+"F0.imprint","IMPRINT",EDGE,{"disambiguationData":[TD([[subQ2,-1.0]])],"derivedFrom":subQ1}),-1.0]])]});}
            var Q14;
            {var subQ6=sQuery(id+"F0.wireOp",EDGE,"E1.left");Q14=makeQuery(id+"F0.imprint","IMPRINT",FACE,{"disambiguationData":[TD([[makeQuery(id+"F0.imprint","IMPRINT",EDGE,{"derivedFrom":subQ6}),1.0]])]});}
            extrude(context, id + "F4", {"entities" : qUnion([Q0, Q1, Q2, Q3, Q4, Q5, Q6, Q7, Q8, Q9, Q10, Q11, Q12, Q13, Q14]), "depth" : 3 * mm, "offsetDistance" : 25 * mm});
        }
        {
            var Q0;
            Q0=makeQuery(id+"F4.opExtrude","CAP_FACE",FACE,{"disambiguationData":[OSD([sQuery(id+"F0.wireOp",EDGE,"E1.bottom"),sQuery(id+"F0.wireOp",EDGE,"E1.top"),sQuery(id+"F0.wireOp",EDGE,"E1.left"),sQuery(id+"F0.wireOp",EDGE,"E1.right")])],"isStart":false});
            var Q1;
            Q1=makeQuery(id+"F4.opExtrude","CAP_FACE",FACE,{"disambiguationData":[OSD([sQuery(id+"F0.wireOp",EDGE,"E0.top"),sQuery(id+"F0.wireOp",EDGE,"E18"),sQuery(id+"F0.wireOp",EDGE,"E27"),sQuery(id+"F0.wireOp",EDGE,"E34.MirrorCS"),sQuery(id+"F0.wireOp",EDGE,"E36.MirrorCS")])],"isStart":false});
            var Q2;
            Q2=makeQuery(id+"F4.opExtrude","CAP_FACE",FACE,{"disambiguationData":[OSD([sQuery(id+"F0.wireOp",EDGE,"E0.top"),sQuery(id+"F0.wireOp",EDGE,"E27"),sQuery(id+"F0.wireOp",EDGE,"E28"),sQuery(id+"F0.wireOp",EDGE,"E33.MirrorCS"),sQuery(id+"F0.wireOp",EDGE,"E34.MirrorCS")])],"isStart":false});
            var Q3;
            Q3=makeQuery(id+"F4.opExtrude","CAP_FACE",FACE,{"disambiguationData":[OSD([sQuery(id+"F0.wireOp",EDGE,"E0.top"),sQuery(id+"F0.wireOp",EDGE,"E28"),sQuery(id+"F0.wireOp",EDGE,"E29"),sQuery(id+"F0.wireOp",EDGE,"E32.MirrorCS"),sQuery(id+"F0.wireOp",EDGE,"E33.MirrorCS")])],"isStart":false});
            var Q4;
            Q4=makeQuery(id+"F4.opExtrude","CAP_FACE",FACE,{"disambiguationData":[OSD([sQuery(id+"F0.wireOp",EDGE,"E0.top"),sQuery(id+"F0.wireOp",EDGE,"E20.MirrorCS"),sQuery(id+"F0.wireOp",EDGE,"E29"),sQuery(id+"F0.wireOp",EDGE,"E30"),sQuery(id+"F0.wireOp",EDGE,"E32.MirrorCS")])],"isStart":false});
            var Q5;
            Q5=makeQuery(id+"F4.opExtrude","CAP_FACE",FACE,{"disambiguationData":[OSD([sQuery(id+"F0.wireOp",EDGE,"E19"),sQuery(id+"F0.wireOp",EDGE,"E29"),sQuery(id+"F0.wireOp",EDGE,"E30"),sQuery(id+"F0.wireOp",EDGE,"E33.MirrorCS")])],"isStart":false});
            var Q6;
            Q6=makeQuery(id+"F4.opExtrude","CAP_FACE",FACE,{"disambiguationData":[OSD([sQuery(id+"F0.wireOp",EDGE,"E19"),sQuery(id+"F0.wireOp",EDGE,"E28"),sQuery(id+"F0.wireOp",EDGE,"E34.MirrorCS"),sQuery(id+"F0.wireOp",EDGE,"E36.MirrorCS")])],"isStart":false});
            var Q7;
            Q7=makeQuery(id+"F4.opExtrude","CAP_FACE",FACE,{"disambiguationData":[OSD([sQuery(id+"F0.wireOp",EDGE,"E27"),sQuery(id+"F0.wireOp",EDGE,"E28"),sQuery(id+"F0.wireOp",EDGE,"E35.MirrorCS"),sQuery(id+"F0.wireOp",EDGE,"E36.MirrorCS")])],"isStart":false});
            var Q8;
            Q8=makeQuery(id+"F4.opExtrude","CAP_FACE",FACE,{"disambiguationData":[OSD([sQuery(id+"F0.wireOp",EDGE,"E18"),sQuery(id+"F0.wireOp",EDGE,"E27"),sQuery(id+"F0.wireOp",EDGE,"E35.MirrorCS"),sQuery(id+"F0.wireOp",EDGE,"E39.MirrorCS")])],"isStart":false});
            var Q9;
            Q9=makeQuery(id+"F4.opExtrude","CAP_FACE",FACE,{"disambiguationData":[OSD([sQuery(id+"F0.wireOp",EDGE,"E30"),sQuery(id+"F0.wireOp",EDGE,"E31"),sQuery(id+"F0.wireOp",EDGE,"E32.MirrorCS"),sQuery(id+"F0.wireOp",EDGE,"E33.MirrorCS")])],"isStart":false});
            var Q10;
            Q10=makeQuery(id+"F4.opExtrude","CAP_FACE",FACE,{"disambiguationData":[OSD([sQuery(id+"F0.wireOp",EDGE,"E20.MirrorCS"),sQuery(id+"F0.wireOp",EDGE,"E31"),sQuery(id+"F0.wireOp",EDGE,"E32.MirrorCS"),sQuery(id+"F0.wireOp",EDGE,"E38")])],"isStart":false});
            var Q11;
            Q11=makeQuery(id+"F4.opExtrude","CAP_FACE",FACE,{"disambiguationData":[OSD([sQuery(id+"F0.wireOp",EDGE,"E20.MirrorCS"),sQuery(id+"F0.wireOp",EDGE,"E32.MirrorCS"),sQuery(id+"F0.wireOp",EDGE,"E37"),sQuery(id+"F0.wireOp",EDGE,"E38")])],"isStart":false});
            var Q12;
            Q12=makeQuery(id+"F4.opExtrude","CAP_FACE",FACE,{"disambiguationData":[OSD([sQuery(id+"F0.wireOp",EDGE,"E19"),sQuery(id+"F0.wireOp",EDGE,"E31"),sQuery(id+"F0.wireOp",EDGE,"E33.MirrorCS"),sQuery(id+"F0.wireOp",EDGE,"E37")])],"isStart":false});
            var Q13;
            Q13=makeQuery(id+"F4.opExtrude","CAP_FACE",FACE,{"disambiguationData":[OSD([sQuery(id+"F0.wireOp",EDGE,"E19"),sQuery(id+"F0.wireOp",EDGE,"E22.bottom"),sQuery(id+"F0.wireOp",EDGE,"E28"),sQuery(id+"F0.wireOp",EDGE,"E35.MirrorCS")])],"isStart":false});
            var Q14;
            Q14=makeQuery(id+"F4.opExtrude","CAP_FACE",FACE,{"disambiguationData":[OSD([sQuery(id+"F0.wireOp",EDGE,"E18"),sQuery(id+"F0.wireOp",EDGE,"E22.bottom"),sQuery(id+"F0.wireOp",EDGE,"E27"),sQuery(id+"F0.wireOp",EDGE,"E39.MirrorCS")])],"isStart":false});
            shell(context, id + "F5", {"entities" : qUnion([Q0, Q1, Q2, Q3, Q4, Q5, Q6, Q7, Q8, Q9, Q10, Q11, Q12, Q13, Q14]), "thickness" : 0.2 * mm, "oppositeDirection" : true});
        }
        {
            var Q0;
            {var subQ0=sQuery(id+"F0.wireOp",EDGE,"E40");var subQ1=sQuery(id+"F0.wireOp",EDGE,"E2");var subQ2=makeQuery(id+"F0.imprint","INTERSECT",VERTEX,{"derivedFrom":[subQ1,subQ0]});Q0=makeQuery(id+"F0.imprint","IMPRINT",FACE,{"disambiguationData":[TD([[makeQuery(id+"F0.imprint","IMPRINT",EDGE,{"disambiguationData":[TD([[subQ2,-1.0]])],"derivedFrom":subQ1}),-1.0]])]});}
            var Q1;
            {var subQ7=sQuery(id+"F0.wireOp",EDGE,"E43");var subQ8=sQuery(id+"F0.wireOp",EDGE,"E3.MirrorCS");var subQ9=makeQuery(id+"F0.imprint","INTERSECT",VERTEX,{"derivedFrom":[subQ8,subQ7]});Q1=makeQuery(id+"F0.imprint","IMPRINT",FACE,{"disambiguationData":[TD([[makeQuery(id+"F0.imprint","IMPRINT",EDGE,{"disambiguationData":[TD([[subQ9,1.0]])],"derivedFrom":subQ8}),1.0]])]});}
            var Q2;
            {var subQ0=sQuery(id+"F0.wireOp",EDGE,"E42");var subQ1=sQuery(id+"F0.wireOp",EDGE,"E1.top");var subQ2=makeQuery(id+"F0.imprint","INTERSECT",VERTEX,{"derivedFrom":[subQ1,subQ0]});Q2=makeQuery(id+"F0.imprint","IMPRINT",FACE,{"disambiguationData":[TD([[makeQuery(id+"F0.imprint","IMPRINT",EDGE,{"disambiguationData":[TD([[subQ2,-1.0]])],"derivedFrom":subQ1}),-1.0]])]});}
            var Q3;
            {var subQ0=sQuery(id+"F0.wireOp",EDGE,"E46.MirrorCS");var subQ1=sQuery(id+"F0.wireOp",EDGE,"E1.top");var subQ2=makeQuery(id+"F0.imprint","INTERSECT",VERTEX,{"derivedFrom":[subQ1,subQ0]});Q3=makeQuery(id+"F0.imprint","IMPRINT",FACE,{"disambiguationData":[TD([[makeQuery(id+"F0.imprint","IMPRINT",EDGE,{"disambiguationData":[TD([[subQ2,-1.0]])],"derivedFrom":subQ1}),-1.0]])]});}
            var Q4;
            {var subQ0=sQuery(id+"F0.wireOp",EDGE,"E54.MirrorCS");var subQ1=sQuery(id+"F0.wireOp",EDGE,"E1.bottom");var subQ2=makeQuery(id+"F0.imprint","INTERSECT",VERTEX,{"derivedFrom":[subQ1,subQ0]});Q4=makeQuery(id+"F0.imprint","IMPRINT",FACE,{"disambiguationData":[TD([[makeQuery(id+"F0.imprint","IMPRINT",EDGE,{"disambiguationData":[TD([[subQ2,1.0]])],"derivedFrom":subQ1}),1.0]])]});}
            var Q5;
            {var subQ0=sQuery(id+"F0.wireOp",EDGE,"E50");var subQ1=sQuery(id+"F0.wireOp",EDGE,"E1.bottom");var subQ2=makeQuery(id+"F0.imprint","INTERSECT",VERTEX,{"derivedFrom":[subQ1,subQ0]});Q5=makeQuery(id+"F0.imprint","IMPRINT",FACE,{"disambiguationData":[TD([[makeQuery(id+"F0.imprint","IMPRINT",EDGE,{"disambiguationData":[TD([[subQ2,-1.0]])],"derivedFrom":subQ1}),1.0]])]});}
            var Q6;
            {var subQ0=sQuery(id+"F0.wireOp",EDGE,"E51");var subQ1=sQuery(id+"F0.wireOp",EDGE,"E17.MirrorCS");var subQ2=makeQuery(id+"F0.imprint","INTERSECT",VERTEX,{"derivedFrom":[subQ1,subQ0]});Q6=makeQuery(id+"F0.imprint","IMPRINT",FACE,{"disambiguationData":[TD([[makeQuery(id+"F0.imprint","IMPRINT",EDGE,{"disambiguationData":[TD([[subQ2,-1.0]])],"derivedFrom":subQ1}),1.0]])]});}
            var Q7;
            {var subQ0=sQuery(id+"F0.wireOp",EDGE,"E51");var subQ1=sQuery(id+"F0.wireOp",EDGE,"E16");var subQ2=makeQuery(id+"F0.imprint","INTERSECT",VERTEX,{"derivedFrom":[subQ1,subQ0]});Q7=makeQuery(id+"F0.imprint","IMPRINT",FACE,{"disambiguationData":[TD([[makeQuery(id+"F0.imprint","IMPRINT",EDGE,{"disambiguationData":[TD([[subQ2,1.0]])],"derivedFrom":subQ1}),-1.0]])]});}
            var Q8;
            {var subQ0=sQuery(id+"F0.wireOp",EDGE,"E53.MirrorCS");var subQ1=sQuery(id+"F0.wireOp",EDGE,"E16");var subQ2=makeQuery(id+"F0.imprint","INTERSECT",VERTEX,{"derivedFrom":[subQ1,subQ0]});Q8=makeQuery(id+"F0.imprint","IMPRINT",FACE,{"disambiguationData":[TD([[makeQuery(id+"F0.imprint","IMPRINT",EDGE,{"disambiguationData":[TD([[subQ2,-1.0]])],"derivedFrom":subQ1}),-1.0]])]});}
            var Q9;
            Q9=makeQuery(id+"F0.imprint","IMPRINT",FACE,{"disambiguationData":[TD([[makeQuery(id+"F0.imprint","IMPRINT",EDGE,{"derivedFrom":sQuery(id+"F0.wireOp",EDGE,"E9")}),1.0]])]});
            var Q10;
            {var subQ0=sQuery(id+"F0.wireOp",EDGE,"E52");var subQ1=sQuery(id+"F0.wireOp",EDGE,"E17.MirrorCS");var subQ2=makeQuery(id+"F0.imprint","INTERSECT",VERTEX,{"derivedFrom":[subQ1,subQ0]});Q10=makeQuery(id+"F0.imprint","IMPRINT",FACE,{"disambiguationData":[TD([[makeQuery(id+"F0.imprint","IMPRINT",EDGE,{"disambiguationData":[TD([[subQ2,-1.0]])],"derivedFrom":subQ1}),1.0]])]});}
            extrude(context, id + "F6", {"entities" : qUnion([Q0, Q1, Q2, Q3, Q4, Q5, Q6, Q7, Q8, Q9, Q10]), "depth" : 3 * mm, "offsetDistance" : 25 * mm});
        }
        {
            var Q0;
            Q0=makeQuery(id+"F6.opExtrude","CAP_FACE",FACE,{"disambiguationData":[OSD([sQuery(id+"F0.wireOp",EDGE,"E16"),sQuery(id+"F0.wireOp",EDGE,"E52"),sQuery(id+"F0.wireOp",EDGE,"E53.MirrorCS")])],"isStart":false});
            var Q1;
            Q1=makeQuery(id+"F6.opExtrude","CAP_FACE",FACE,{"disambiguationData":[OSD([sQuery(id+"F0.wireOp",EDGE,"E8"),sQuery(id+"F0.wireOp",EDGE,"E9"),sQuery(id+"F0.wireOp",EDGE,"E10"),sQuery(id+"F0.wireOp",EDGE,"E11")])],"isStart":false});
            var Q2;
            Q2=makeQuery(id+"F6.opExtrude","CAP_FACE",FACE,{"disambiguationData":[OSD([sQuery(id+"F0.wireOp",EDGE,"E17.MirrorCS"),sQuery(id+"F0.wireOp",EDGE,"E52"),sQuery(id+"F0.wireOp",EDGE,"E53.MirrorCS")])],"isStart":false});
            var Q3;
            Q3=makeQuery(id+"F6.opExtrude","CAP_FACE",FACE,{"disambiguationData":[OSD([sQuery(id+"F0.wireOp",EDGE,"E16"),sQuery(id+"F0.wireOp",EDGE,"E51"),sQuery(id+"F0.wireOp",EDGE,"E55.MirrorCS")])],"isStart":false});
            var Q4;
            Q4=makeQuery(id+"F6.opExtrude","CAP_FACE",FACE,{"disambiguationData":[OSD([sQuery(id+"F0.wireOp",EDGE,"E17.MirrorCS"),sQuery(id+"F0.wireOp",EDGE,"E51"),sQuery(id+"F0.wireOp",EDGE,"E55.MirrorCS")])],"isStart":false});
            var Q5;
            Q5=makeQuery(id+"F6.opExtrude","CAP_FACE",FACE,{"disambiguationData":[OSD([sQuery(id+"F0.wireOp",EDGE,"E1.bottom"),sQuery(id+"F0.wireOp",EDGE,"E16"),sQuery(id+"F0.wireOp",EDGE,"E50"),sQuery(id+"F0.wireOp",EDGE,"E54.MirrorCS")])],"isStart":false});
            var Q6;
            Q6=makeQuery(id+"F6.opExtrude","CAP_FACE",FACE,{"disambiguationData":[OSD([sQuery(id+"F0.wireOp",EDGE,"E1.bottom"),sQuery(id+"F0.wireOp",EDGE,"E17.MirrorCS"),sQuery(id+"F0.wireOp",EDGE,"E50"),sQuery(id+"F0.wireOp",EDGE,"E54.MirrorCS")])],"isStart":false});
            var Q7;
            Q7=makeQuery(id+"F6.opExtrude","CAP_FACE",FACE,{"disambiguationData":[OSD([sQuery(id+"F0.wireOp",EDGE,"E1.top"),sQuery(id+"F0.wireOp",EDGE,"E42"),sQuery(id+"F0.wireOp",EDGE,"E43"),sQuery(id+"F0.wireOp",EDGE,"E46.MirrorCS")])],"isStart":false});
            var Q8;
            Q8=makeQuery(id+"F6.opExtrude","CAP_FACE",FACE,{"disambiguationData":[OSD([sQuery(id+"F0.wireOp",EDGE,"E1.top"),sQuery(id+"F0.wireOp",EDGE,"E43"),sQuery(id+"F0.wireOp",EDGE,"E46.MirrorCS"),sQuery(id+"F0.wireOp",EDGE,"E47.MirrorCS")])],"isStart":false});
            var Q9;
            Q9=makeQuery(id+"F6.opExtrude","CAP_FACE",FACE,{"disambiguationData":[OSD([sQuery(id+"F0.wireOp",EDGE,"E3.MirrorCS"),sQuery(id+"F0.wireOp",EDGE,"E4"),sQuery(id+"F0.wireOp",EDGE,"E43"),sQuery(id+"F0.wireOp",EDGE,"E44"),sQuery(id+"F0.wireOp",EDGE,"E48.MirrorCS"),sQuery(id+"F0.wireOp",EDGE,"E49.MirrorCS")])],"isStart":false});
            var Q10;
            Q10=makeQuery(id+"F6.opExtrude","CAP_FACE",FACE,{"disambiguationData":[OSD([sQuery(id+"F0.wireOp",EDGE,"E2"),sQuery(id+"F0.wireOp",EDGE,"E4"),sQuery(id+"F0.wireOp",EDGE,"E40"),sQuery(id+"F0.wireOp",EDGE,"E41"),sQuery(id+"F0.wireOp",EDGE,"E45.MirrorCS"),sQuery(id+"F0.wireOp",EDGE,"E46.MirrorCS")])],"isStart":false});
            shell(context, id + "F7", {"entities" : qUnion([Q0, Q1, Q2, Q3, Q4, Q5, Q6, Q7, Q8, Q9, Q10]), "thickness" : 0.2 * mm, "oppositeDirection" : true});
        }
        {
            var Q0;
            {var subQ1=sQuery(id+"F0.wireOp",EDGE,"E16");var subQ6=sQuery(id+"F0.wireOp",EDGE,"E7.top");var subQ9=makeQuery(id+"F0.imprint","INTERSECT",VERTEX,{"derivedFrom":[subQ6,subQ1]});Q0=makeQuery(id+"F0.imprint","IMPRINT",FACE,{"disambiguationData":[TD([[makeQuery(id+"F0.imprint","IMPRINT",EDGE,{"disambiguationData":[TD([[subQ9,-1.0]])],"derivedFrom":subQ6}),-1.0]])]});}
            var Q1;
            {var subQ0=sQuery(id+"F0.wireOp",EDGE,"E44");var subQ1=sQuery(id+"F0.wireOp",EDGE,"E4");var subQ2=makeQuery(id+"F0.imprint","INTERSECT",VERTEX,{"derivedFrom":[subQ1,subQ0]});Q1=makeQuery(id+"F0.imprint","IMPRINT",FACE,{"disambiguationData":[TD([[makeQuery(id+"F0.imprint","IMPRINT",EDGE,{"disambiguationData":[TD([[subQ2,-1.0]])],"derivedFrom":subQ1}),1.0]])]});}
            var Q2;
            {var subQ0=sQuery(id+"F0.wireOp",EDGE,"E3.MirrorCS");var subQ1=sQuery(id+"F0.wireOp",EDGE,"E0.bottom");var subQ2=makeQuery(id+"F0.imprint","INTERSECT",VERTEX,{"derivedFrom":[subQ1,subQ0]});Q2=makeQuery(id+"F0.imprint","IMPRINT",FACE,{"disambiguationData":[TD([[makeQuery(id+"F0.imprint","IMPRINT",EDGE,{"disambiguationData":[TD([[subQ2,1.0]])],"derivedFrom":subQ1}),1.0]])]});}
            var Q3;
            {var subQ0=sQuery(id+"F0.wireOp",EDGE,"E43");var subQ1=sQuery(id+"F0.wireOp",EDGE,"E3.MirrorCS");var subQ2=makeQuery(id+"F0.imprint","INTERSECT",VERTEX,{"derivedFrom":[subQ1,subQ0]});Q3=makeQuery(id+"F0.imprint","IMPRINT",FACE,{"disambiguationData":[TD([[makeQuery(id+"F0.imprint","IMPRINT",EDGE,{"disambiguationData":[TD([[subQ2,-1.0]])],"derivedFrom":subQ1}),1.0]])]});}
            var Q4;
            {var subQ5=sQuery(id+"F0.wireOp",EDGE,"E42");var subQ7=sQuery(id+"F0.wireOp",EDGE,"E4");var subQ8=makeQuery(id+"F0.imprint","INTERSECT",VERTEX,{"derivedFrom":[subQ7,subQ5]});Q4=makeQuery(id+"F0.imprint","IMPRINT",FACE,{"disambiguationData":[TD([[makeQuery(id+"F0.imprint","IMPRINT",EDGE,{"disambiguationData":[TD([[subQ8,-1.0]])],"derivedFrom":subQ7}),1.0]])]});}
            var Q5;
            {var subQ4=sQuery(id+"F0.wireOp",EDGE,"E41");var subQ6=sQuery(id+"F0.wireOp",EDGE,"E4");var subQ8=makeQuery(id+"F0.imprint","INTERSECT",VERTEX,{"derivedFrom":[subQ6,subQ4]});Q5=makeQuery(id+"F0.imprint","IMPRINT",FACE,{"disambiguationData":[TD([[makeQuery(id+"F0.imprint","IMPRINT",EDGE,{"disambiguationData":[TD([[subQ8,-1.0]])],"derivedFrom":subQ6}),1.0]])]});}
            var Q6;
            {var subQ0=sQuery(id+"F0.wireOp",EDGE,"E41");var subQ1=sQuery(id+"F0.wireOp",EDGE,"E2");var subQ2=makeQuery(id+"F0.imprint","INTERSECT",VERTEX,{"derivedFrom":[subQ1,subQ0]});Q6=makeQuery(id+"F0.imprint","IMPRINT",FACE,{"disambiguationData":[TD([[makeQuery(id+"F0.imprint","IMPRINT",EDGE,{"disambiguationData":[TD([[subQ2,1.0]])],"derivedFrom":subQ1}),-1.0]])]});}
            var Q7;
            {var subQ0=sQuery(id+"F0.wireOp",EDGE,"E45.MirrorCS");var subQ1=sQuery(id+"F0.wireOp",EDGE,"E4");var subQ2=makeQuery(id+"F0.imprint","INTERSECT",VERTEX,{"derivedFrom":[subQ1,subQ0]});Q7=makeQuery(id+"F0.imprint","IMPRINT",FACE,{"disambiguationData":[TD([[makeQuery(id+"F0.imprint","IMPRINT",EDGE,{"disambiguationData":[TD([[subQ2,1.0]])],"derivedFrom":subQ1}),1.0]])]});}
            var Q8;
            {var subQ0=sQuery(id+"F0.wireOp",EDGE,"E2");var subQ1=sQuery(id+"F0.wireOp",EDGE,"E0.bottom");var subQ2=makeQuery(id+"F0.imprint","INTERSECT",VERTEX,{"derivedFrom":[subQ1,subQ0]});Q8=makeQuery(id+"F0.imprint","IMPRINT",FACE,{"disambiguationData":[TD([[makeQuery(id+"F0.imprint","IMPRINT",EDGE,{"disambiguationData":[TD([[subQ2,-1.0]])],"derivedFrom":subQ1}),1.0]])]});}
            var Q9;
            {var subQ0=sQuery(id+"F0.wireOp",EDGE,"E0.left");Q9=makeQuery(id+"F0.imprint","IMPRINT",FACE,{"disambiguationData":[TD([[makeQuery(id+"F0.imprint","IMPRINT",EDGE,{"derivedFrom":subQ0}),1.0]])]});}
            extrude(context, id + "F8", {"entities" : qUnion([Q0, Q1, Q2, Q3, Q4, Q5, Q6, Q7, Q8, Q9]), "depth" : 3 * mm, "offsetDistance" : 25 * mm});
        }
        {
            var Q0;
            Q0=makeQuery(id+"F8.opExtrude","CAP_FACE",FACE,{"disambiguationData":[OSD([sQuery(id+"F0.wireOp",EDGE,"E4"),sQuery(id+"F0.wireOp",EDGE,"E40"),sQuery(id+"F0.wireOp",EDGE,"E45.MirrorCS")])],"isStart":false});
            var Q1;
            Q1=makeQuery(id+"F8.opExtrude","CAP_FACE",FACE,{"disambiguationData":[OSD([sQuery(id+"F0.wireOp",EDGE,"E4"),sQuery(id+"F0.wireOp",EDGE,"E41"),sQuery(id+"F0.wireOp",EDGE,"E42"),sQuery(id+"F0.wireOp",EDGE,"E43"),sQuery(id+"F0.wireOp",EDGE,"E46.MirrorCS"),sQuery(id+"F0.wireOp",EDGE,"E47.MirrorCS"),sQuery(id+"F0.wireOp",EDGE,"E48.MirrorCS")])],"isStart":false});
            var Q2;
            Q2=makeQuery(id+"F8.opExtrude","CAP_FACE",FACE,{"disambiguationData":[OSD([sQuery(id+"F0.wireOp",EDGE,"E4"),sQuery(id+"F0.wireOp",EDGE,"E44"),sQuery(id+"F0.wireOp",EDGE,"E49.MirrorCS")])],"isStart":false});
            var Q3;
            Q3=makeQuery(id+"F8.opExtrude","CAP_FACE",FACE,{"disambiguationData":[OSD([sQuery(id+"F0.wireOp",EDGE,"E7.top"),sQuery(id+"F0.wireOp",EDGE,"E16"),sQuery(id+"F0.wireOp",EDGE,"E17.MirrorCS"),sQuery(id+"F0.wireOp",EDGE,"E52"),sQuery(id+"F0.wireOp",EDGE,"E53.MirrorCS")])],"isStart":false});
            var Q4;
            Q4=makeQuery(id+"F8.opExtrude","CAP_FACE",FACE,{"disambiguationData":[OSD([sQuery(id+"F0.wireOp",EDGE,"E0.bottom"),sQuery(id+"F0.wireOp",EDGE,"E0.top"),sQuery(id+"F0.wireOp",EDGE,"E0.left"),sQuery(id+"F0.wireOp",EDGE,"E0.right"),sQuery(id+"F0.wireOp",EDGE,"E2"),sQuery(id+"F0.wireOp",EDGE,"E3.MirrorCS"),sQuery(id+"F0.wireOp",EDGE,"E40"),sQuery(id+"F0.wireOp",EDGE,"E44"),sQuery(id+"F0.wireOp",EDGE,"E45.MirrorCS"),sQuery(id+"F0.wireOp",EDGE,"E49.MirrorCS")])],"isStart":false});
            var Q5;
            Q5=makeQuery(id+"F8.opExtrude","CAP_FACE",FACE,{"disambiguationData":[OSD([sQuery(id+"F0.wireOp",EDGE,"E2"),sQuery(id+"F0.wireOp",EDGE,"E41"),sQuery(id+"F0.wireOp",EDGE,"E46.MirrorCS")])],"isStart":false});
            var Q6;
            Q6=makeQuery(id+"F8.opExtrude","CAP_FACE",FACE,{"disambiguationData":[OSD([sQuery(id+"F0.wireOp",EDGE,"E3.MirrorCS"),sQuery(id+"F0.wireOp",EDGE,"E43"),sQuery(id+"F0.wireOp",EDGE,"E48.MirrorCS")])],"isStart":false});
            shell(context, id + "F9", {"entities" : qUnion([Q0, Q1, Q2, Q3, Q4, Q5, Q6]), "thickness" : 0.2 * mm, "oppositeDirection" : true});
        }
        {
            var Q0;
            {var subQ37=sQuery(id+"F0.wireOp",EDGE,"E0.left");Q0=makeQuery(id+"F0.imprint","IMPRINT",FACE,{"disambiguationData":[TD([[makeQuery(id+"F0.imprint","IMPRINT",EDGE,{"derivedFrom":subQ37}),-1.0]])]});}
            extrude(context, id + "F10", {"entities" : qUnion([Q0]), "oppositeDirection" : true, "depth" : 12 * mm, "offsetDistance" : 25 * mm});
        }
        {
            var Q0;
            Q0=makeQuery(id+"F10.opExtrude","CAP_EDGE",EDGE,{"disambiguationData":[OSD([sQuery(id+"F0.wireOp",EDGE,"E56.left")])],"isStart":false});
            var Q1;
            Q1=makeQuery(id+"F10.opExtrude","CAP_EDGE",EDGE,{"disambiguationData":[OSD([sQuery(id+"F0.wireOp",EDGE,"E56.bottom")])],"isStart":false});
            var Q2;
            Q2=makeQuery(id+"F10.opExtrude","CAP_EDGE",EDGE,{"disambiguationData":[OSD([sQuery(id+"F0.wireOp",EDGE,"E56.right")])],"isStart":false});
            var Q3;
            Q3=makeQuery(id+"F10.opExtrude","CAP_EDGE",EDGE,{"disambiguationData":[OSD([sQuery(id+"F0.wireOp",EDGE,"E56.top")])],"isStart":false});
            fillet(context, id + "F11", {"entities" : qUnion([Q0, Q1, Q2, Q3]), "radius" : 10 * mm, "tangentPropagation" : true, "allowEdgeOverflow" : false});
        }
    });
